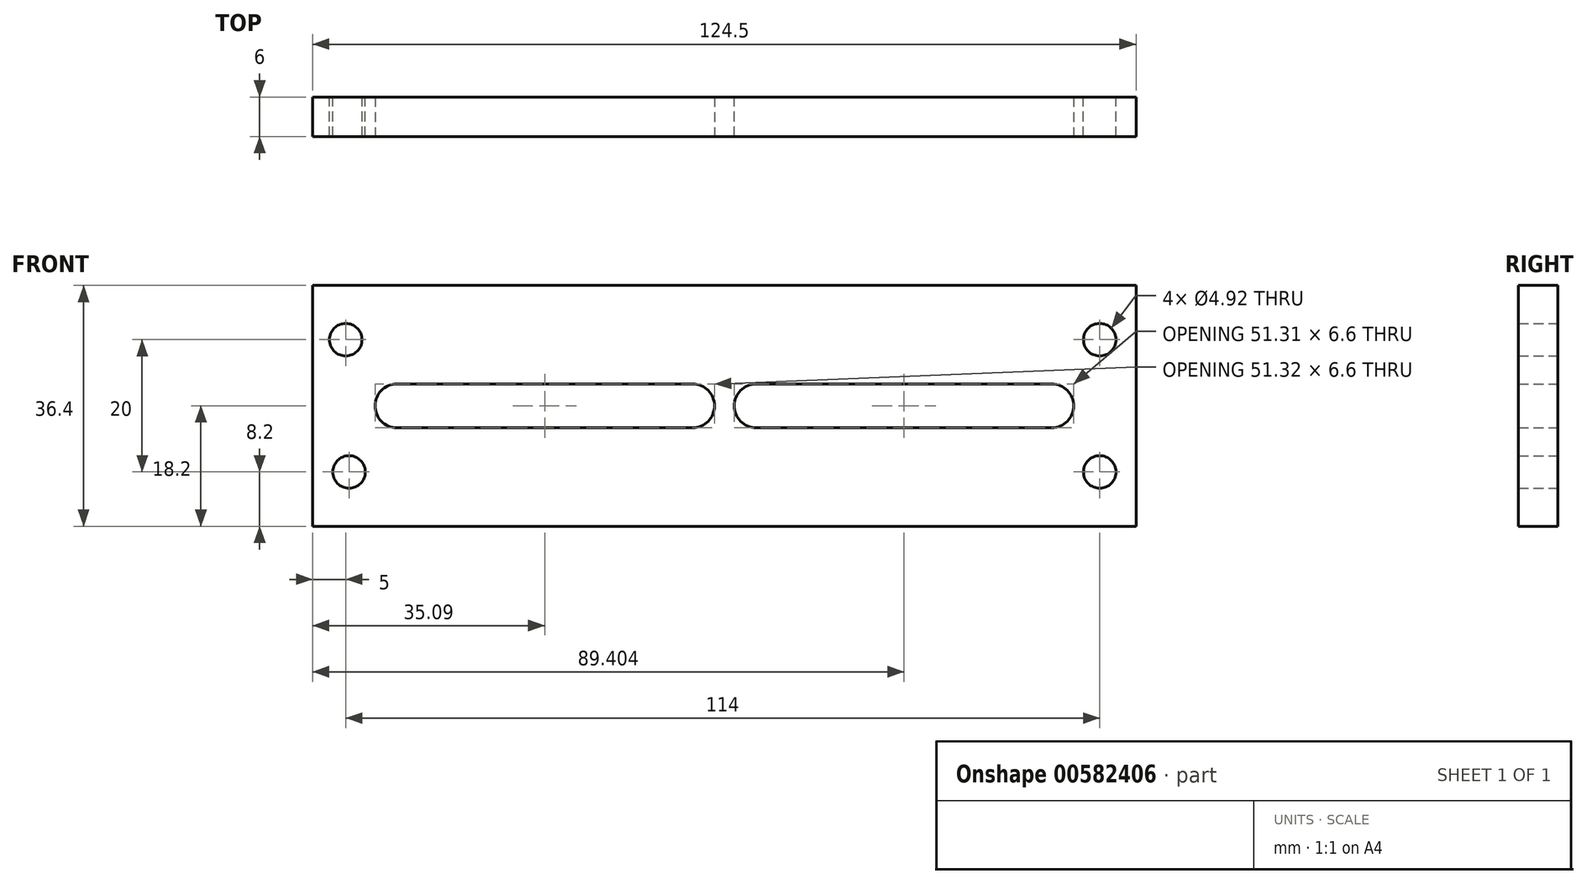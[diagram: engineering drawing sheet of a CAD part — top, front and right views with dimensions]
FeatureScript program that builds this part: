
annotation { "Feature Type Name" : "Feature", "Feature Type Description" : "" }
export const myFeature = defineFeature(function(context is Context, id is Id, definition is map)
    precondition{}
    {
        {
            var Q0;
            Q0=qCreatedBy(makeId("Front.planeOp"),FACE);
            var sketch = newSketch(context, id + "F0", { "sketchPlane" : qUnion([Q0])});
            skLineSegment(sketch, "E0.bottom", {"start": v(-62.25, 18.2) * mm, "end": v(62.25, 18.2) * mm});
            skLineSegment(sketch, "E0.top", {"start": v(-62.25, -18.2) * mm, "end": v(62.25, -18.2) * mm});
            skLineSegment(sketch, "E0.left", {"start": v(-62.25, 18.2) * mm, "end": v(-62.25, -18.2) * mm});
            skLineSegment(sketch, "E0.right", {"start": v(62.25, 18.2) * mm, "end": v(62.25, -18.2) * mm});
            skPoint(sketch, "E0.middle", {"position": v(0, 0) * mm});
            skLineSegment(sketch, "E1.bottom", {"start": v(-52.82, 3.3) * mm, "end": v(-1.5, 3.3) * mm});
            skLineSegment(sketch, "E1.top", {"start": v(-52.82, -3.3) * mm, "end": v(-1.5, -3.3) * mm});
            skLineSegment(sketch, "E1.left", {"start": v(-52.82, 3.3) * mm, "end": v(-52.82, -3.3) * mm});
            skLineSegment(sketch, "E1.right", {"start": v(-1.5, 3.3) * mm, "end": v(-1.5, -3.3) * mm});
            skLineSegment(sketch, "E2.bottom", {"start": v(1.5, 3.3) * mm, "end": v(52.8, 3.3) * mm});
            skLineSegment(sketch, "E2.top", {"start": v(1.5, -3.3) * mm, "end": v(52.8, -3.3) * mm});
            skLineSegment(sketch, "E2.left", {"start": v(1.5, 3.3) * mm, "end": v(1.5, -3.3) * mm});
            skLineSegment(sketch, "E2.right", {"start": v(52.8, 3.3) * mm, "end": v(52.8, -3.3) * mm});
            skCircle(sketch, "E3", {"center": v(-57.25, 10) * mm, "radius": 2.46 * mm});
            skCircle(sketch, "E4", {"center": v(56.75, 10) * mm, "radius": 2.46 * mm});
            skCircle(sketch, "E5", {"center": v(56.75, -10) * mm, "radius": 2.46 * mm});
            skCircle(sketch, "E6", {"center": v(-56.75, -10) * mm, "radius": 2.46 * mm});
            skPoint(sketch, "E7.centerSnap0", {"position": v(-52.82, 0) * mm});
            skSolve(sketch);
        }
        {
            var Q0;
            Q0 = qSketchRegion(id + "F0", true);
            extrude(context, id + "F1", {"entities" : qUnion([Q0]), "depth" : 6 * mm, "offsetDistance" : 25.4 * mm});
        }
        {
            var Q0;
            Q0=makeQuery(id+"F1.opExtrude","SWEPT_EDGE",EDGE,{"disambiguationData":[OSD([sQuery(id+"F0.wireOp",EDGE,"E1.top"),sQuery(id+"F0.wireOp",EDGE,"E1.left")])]});
            fillet(context, id + "F2", {"entities" : qUnion([Q0]), "radius" : 3.3 * mm, "tangentPropagation" : true, "allowEdgeOverflow" : false});
        }
        {
            var Q0;
            Q0=makeQuery(id+"F1.opExtrude","SWEPT_EDGE",EDGE,{"disambiguationData":[OSD([sQuery(id+"F0.wireOp",EDGE,"E1.bottom"),sQuery(id+"F0.wireOp",EDGE,"E1.left")])]});
            fillet(context, id + "F3", {"entities" : qUnion([Q0]), "radius" : 3.3 * mm, "tangentPropagation" : true, "allowEdgeOverflow" : false});
        }
        {
            var Q0;
            Q0=makeQuery(id+"F1.opExtrude","SWEPT_EDGE",EDGE,{"disambiguationData":[OSD([sQuery(id+"F0.wireOp",EDGE,"E1.bottom"),sQuery(id+"F0.wireOp",EDGE,"E1.right")])]});
            fillet(context, id + "F4", {"entities" : qUnion([Q0]), "radius" : 3.3 * mm, "tangentPropagation" : true, "allowEdgeOverflow" : false});
        }
        {
            var Q0;
            Q0=makeQuery(id+"F1.opExtrude","SWEPT_EDGE",EDGE,{"disambiguationData":[OSD([sQuery(id+"F0.wireOp",EDGE,"E1.top"),sQuery(id+"F0.wireOp",EDGE,"E1.right")])]});
            fillet(context, id + "F5", {"entities" : qUnion([Q0]), "radius" : 3.3 * mm, "tangentPropagation" : true, "allowEdgeOverflow" : false});
        }
        {
            var Q0;
            Q0=makeQuery(id+"F1.opExtrude","SWEPT_EDGE",EDGE,{"disambiguationData":[OSD([sQuery(id+"F0.wireOp",EDGE,"E2.bottom"),sQuery(id+"F0.wireOp",EDGE,"E2.left")])]});
            fillet(context, id + "F6", {"entities" : qUnion([Q0]), "radius" : 3.3 * mm, "tangentPropagation" : true, "allowEdgeOverflow" : false});
        }
        {
            var Q0;
            Q0=makeQuery(id+"F1.opExtrude","SWEPT_EDGE",EDGE,{"disambiguationData":[OSD([sQuery(id+"F0.wireOp",EDGE,"E2.top"),sQuery(id+"F0.wireOp",EDGE,"E2.left")])]});
            fillet(context, id + "F7", {"entities" : qUnion([Q0]), "radius" : 3.3 * mm, "tangentPropagation" : true, "allowEdgeOverflow" : false});
        }
        {
            var Q0;
            Q0=makeQuery(id+"F1.opExtrude","SWEPT_EDGE",EDGE,{"disambiguationData":[OSD([sQuery(id+"F0.wireOp",EDGE,"E2.bottom"),sQuery(id+"F0.wireOp",EDGE,"E2.right")])]});
            fillet(context, id + "F8", {"entities" : qUnion([Q0]), "radius" : 3.3 * mm, "tangentPropagation" : true, "allowEdgeOverflow" : false});
        }
        {
            var Q0;
            Q0=makeQuery(id+"F1.opExtrude","SWEPT_EDGE",EDGE,{"disambiguationData":[OSD([sQuery(id+"F0.wireOp",EDGE,"E2.top"),sQuery(id+"F0.wireOp",EDGE,"E2.right")])]});
            fillet(context, id + "F9", {"entities" : qUnion([Q0]), "radius" : 3.3 * mm, "tangentPropagation" : true, "allowEdgeOverflow" : false});
        }
    });
